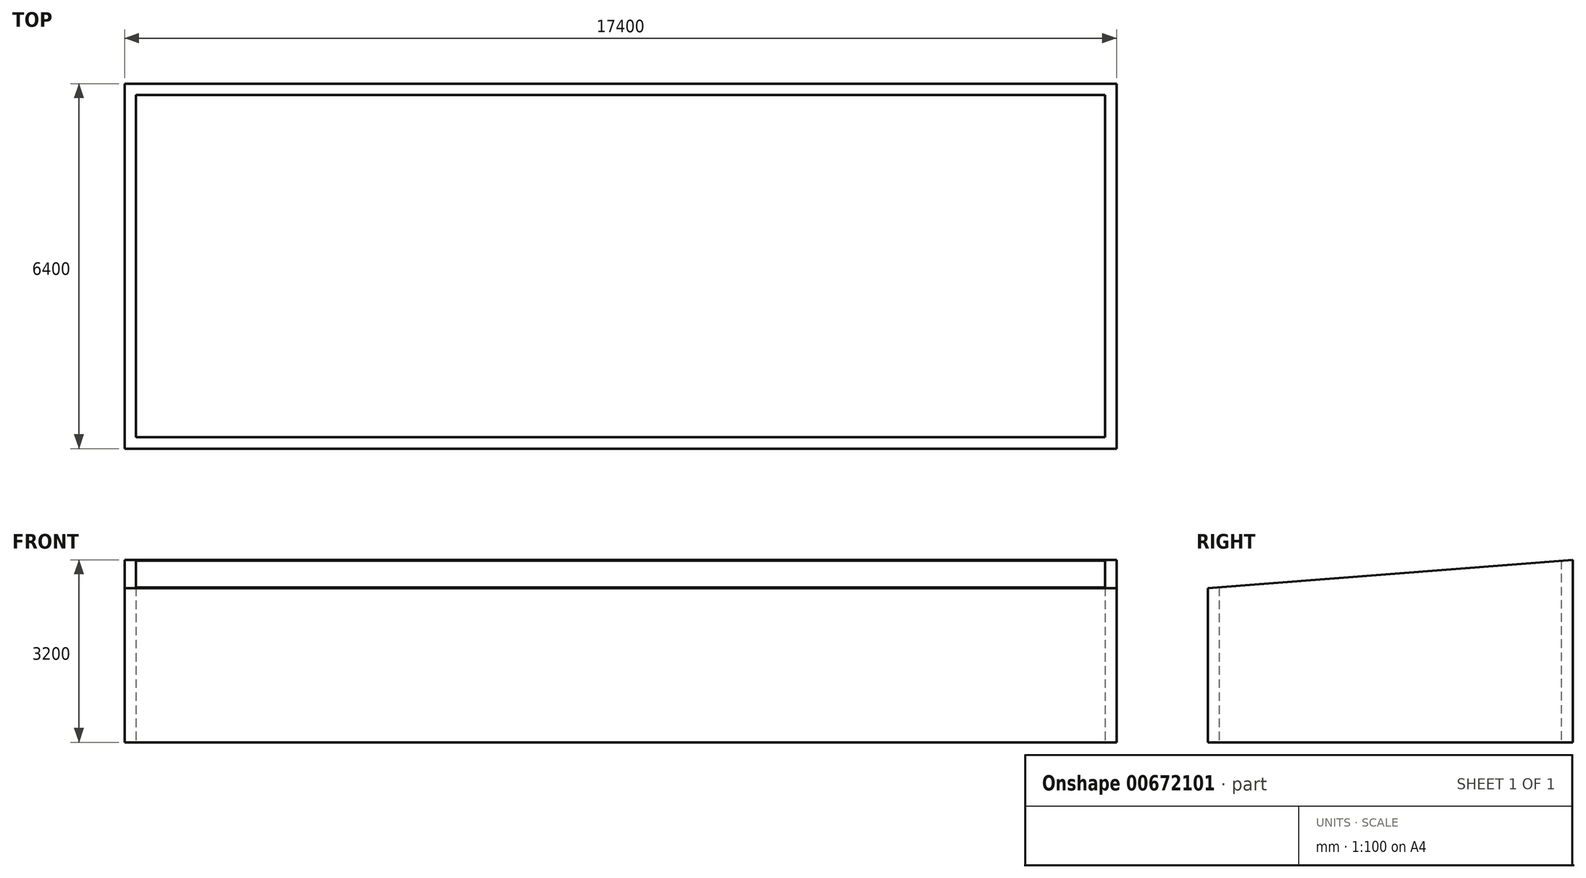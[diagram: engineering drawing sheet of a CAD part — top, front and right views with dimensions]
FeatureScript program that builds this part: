
annotation { "Feature Type Name" : "Feature", "Feature Type Description" : "" }
export const myFeature = defineFeature(function(context is Context, id is Id, definition is map)
    precondition{}
    {
        {
            var Q0;
            Q0=qCreatedBy(makeId("Top.planeOp"),FACE);
            var sketch = newSketch(context, id + "F0", { "sketchPlane" : qUnion([Q0])});
            skLineSegment(sketch, "E0.bottom", {"start": v(-8500, 3000) * mm, "end": v(8500, 3000) * mm});
            skLineSegment(sketch, "E0.top", {"start": v(-8500, -3000) * mm, "end": v(8500, -3000) * mm});
            skLineSegment(sketch, "E0.left", {"start": v(-8500, 3000) * mm, "end": v(-8500, -3000) * mm});
            skLineSegment(sketch, "E0.right", {"start": v(8500, 3000) * mm, "end": v(8500, -3000) * mm});
            skPoint(sketch, "E0.middle", {"position": v(0, 0) * mm});
            skLineSegment(sketch, "E1.0", {"start": v(-8700, 3200) * mm, "end": v(-8700, -3200) * mm});
            skLineSegment(sketch, "E1.1", {"start": v(-8700, 3200) * mm, "end": v(8700, 3200) * mm});
            skLineSegment(sketch, "E1.2", {"start": v(8700, 3200) * mm, "end": v(8700, -3200) * mm});
            skLineSegment(sketch, "E1.3", {"start": v(-8700, -3200) * mm, "end": v(8700, -3200) * mm});
            skSolve(sketch);
        }
        {
            var Q0;
            Q0=makeQuery(id+"F0.imprint","IMPRINT",FACE,{"disambiguationData":[TD([[makeQuery(id+"F0.imprint","IMPRINT",EDGE,{"derivedFrom":sQuery(id+"F0.wireOp",EDGE,"E0.bottom")}),1.0]])]});
            extrude(context, id + "F1", {"entities" : qUnion([Q0]), "depth" : 3200 * mm, "offsetDistance" : 25 * mm});
        }
        {
            var Q0;
            Q0=makeQuery(id+"F1.opExtrude","SWEPT_FACE",FACE,{"disambiguationData":[OSD([sQuery(id+"F0.wireOp",EDGE,"E1.0")])]});
            var sketch = newSketch(context, id + "F2", { "sketchPlane" : qUnion([Q0])});
            skLineSegment(sketch, "E2", {"start": v(3200, 2700) * mm, "end": v(-3200, 3200) * mm});
            skLineSegment(sketch, "E3", {"start": v(-3200, 3200) * mm, "end": v(-3200, 3200) * mm});
            skLineSegment(sketch, "E4", {"start": v(-3200, 3200) * mm, "end": v(3200, 3200) * mm});
            skLineSegment(sketch, "E5", {"start": v(3200, 3200) * mm, "end": v(3200, 2700) * mm});
            skSolve(sketch);
        }
        {
            var Q0;
            Q0 = qSketchRegion(id + "F2", true);
            extrude(context, id + "F3", {"entities" : qUnion([Q0]), "operationType" : NewBodyOperationType.REMOVE, "endBound" : BoundingType.THROUGH_ALL, "oppositeDirection" : true, "depth" : 25 * mm, "offsetDistance" : 25 * mm});
        }
    });
